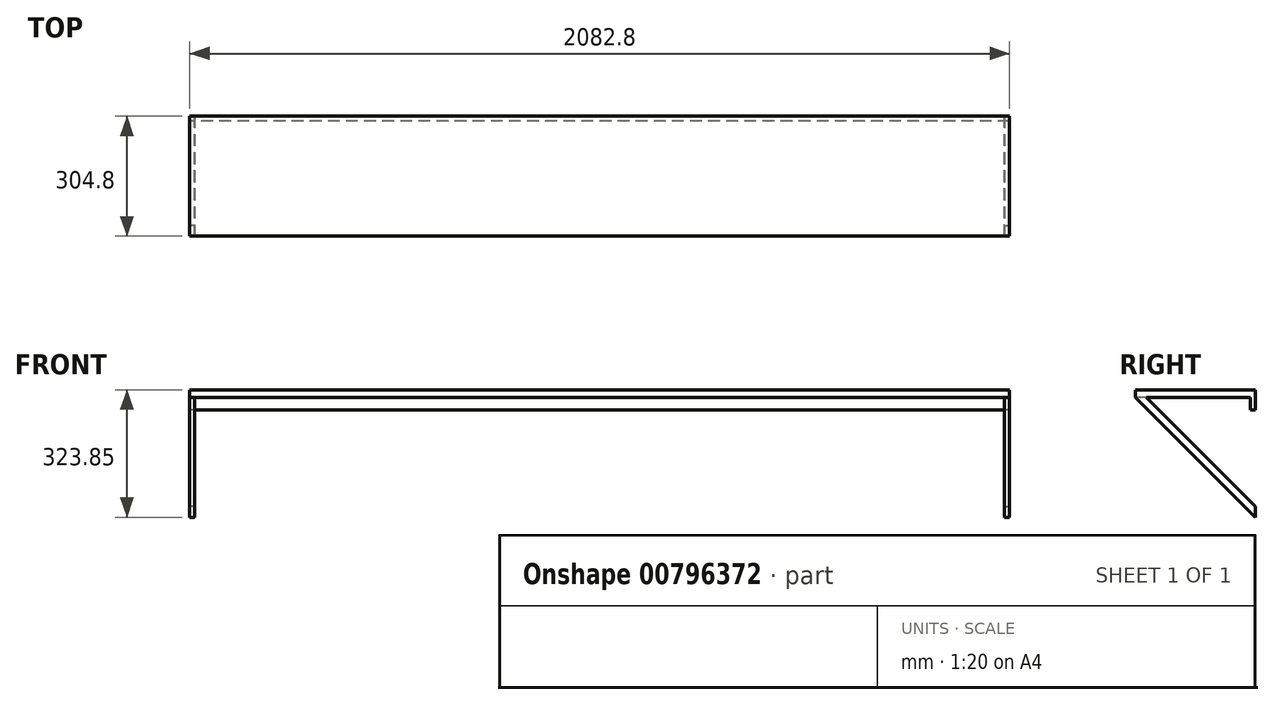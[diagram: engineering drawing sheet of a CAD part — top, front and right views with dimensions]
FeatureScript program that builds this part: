
annotation { "Feature Type Name" : "Feature", "Feature Type Description" : "" }
export const myFeature = defineFeature(function(context is Context, id is Id, definition is map)
    precondition{}
    {
        {
            var Q0;
            Q0=qCreatedBy(makeId("Top.planeOp"),FACE);
            var sketch = newSketch(context, id + "F0", { "sketchPlane" : qUnion([Q0])});
            skLineSegment(sketch, "E0.bottom", {"start": v(0, 0) * mm, "end": v(2082.8, 0) * mm});
            skLineSegment(sketch, "E0.top", {"start": v(0, -304.8) * mm, "end": v(2082.8, -304.8) * mm});
            skLineSegment(sketch, "E0.left", {"start": v(0, 0) * mm, "end": v(0, -304.8) * mm});
            skLineSegment(sketch, "E0.right", {"start": v(2082.8, 0) * mm, "end": v(2082.8, -304.8) * mm});
            skSolve(sketch);
        }
        {
            var Q0;
            Q0=makeQuery(id+"F0.imprint","IMPRINT",FACE,{"disambiguationData":[TD([[makeQuery(id+"F0.imprint","IMPRINT",EDGE,{"derivedFrom":sQuery(id+"F0.wireOp",EDGE,"E0.bottom")}),-1.0]])]});
            extrude(context, id + "F1", {"entities" : qUnion([Q0]), "depth" : 19.05 * mm, "offsetDistance" : 25.4 * mm});
        }
        {
            var Q0;
            Q0=qCreatedBy(makeId("Right.planeOp"),FACE);
            var sketch = newSketch(context, id + "F2", { "sketchPlane" : qUnion([Q0])});
            skLineSegment(sketch, "E1.bottom", {"start": v(0, 0) * mm, "end": v(-12.7, 0) * mm});
            skLineSegment(sketch, "E1.top", {"start": v(0, -31.75) * mm, "end": v(-12.7, -31.75) * mm});
            skLineSegment(sketch, "E1.left", {"start": v(0, 0) * mm, "end": v(0, -31.75) * mm});
            skLineSegment(sketch, "E1.right", {"start": v(-12.7, 0) * mm, "end": v(-12.7, -31.75) * mm});
            skSolve(sketch);
        }
        {
            var Q0;
            Q0=makeQuery(id+"F2.imprint","IMPRINT",FACE,{"disambiguationData":[TD([[makeQuery(id+"F2.imprint","IMPRINT",EDGE,{"derivedFrom":sQuery(id+"F2.wireOp",EDGE,"E1.bottom")}),1.0]])]});
            var Q1;
            Q1=makeQuery(id+"F1.opExtrude","SWEPT_FACE",FACE,{"disambiguationData":[OSD([sQuery(id+"F0.wireOp",EDGE,"E0.right")])]});
            extrude(context, id + "F3", {"entities" : qUnion([Q0]), "operationType" : NewBodyOperationType.ADD, "endBound" : BoundingType.UP_TO_SURFACE, "depth" : 25.4 * mm, "endBoundEntityFace" : qUnion([Q1]), "offsetDistance" : 25.4 * mm});
        }
        {
            var Q0;
            Q0=qCreatedBy(makeId("Right.planeOp"),FACE);
            var sketch = newSketch(context, id + "F4", { "sketchPlane" : qUnion([Q0])});
            skLineSegment(sketch, "E2.0", {"start": v(-12.7, 0) * mm, "end": v(-304.8, 0) * mm, "construction": true});
            skLineSegment(sketch, "E3", {"start": v(-304.8, 0) * mm, "end": v(0, -304.8) * mm});
            skLineSegment(sketch, "E4", {"start": v(0, -304.8) * mm, "end": v(0, -277.86) * mm});
            skLineSegment(sketch, "E5", {"start": v(0, -277.86) * mm, "end": v(-277.86, 0) * mm});
            skLineSegment(sketch, "E6", {"start": v(-277.86, 0) * mm, "end": v(-304.8, 0) * mm});
            skSolve(sketch);
        }
        {
            var Q0;
            Q0=makeQuery(id+"F4.imprint","IMPRINT",FACE,{"disambiguationData":[TD([[makeQuery(id+"F4.imprint","IMPRINT",EDGE,{"derivedFrom":sQuery(id+"F4.wireOp",EDGE,"E3")}),1.0]])]});
            extrude(context, id + "F5", {"entities" : qUnion([Q0]), "operationType" : NewBodyOperationType.ADD, "depth" : 12.7 * mm, "offsetDistance" : 25.4 * mm});
        }
        {
            var Q0;
            Q0=makeQuery(id+"F3.boolean.opBoolean","MERGE",FACE,{"derivedFrom":[makeQuery(id+"F1.opExtrude","SWEPT_FACE",FACE,{"disambiguationData":[OSD([sQuery(id+"F0.wireOp",EDGE,"E0.right")])]}),makeQuery(id+"F3.opExtrude","CAP_FACE",FACE,{"disambiguationData":[OSD([sQuery(id+"F2.wireOp",EDGE,"E1.bottom"),sQuery(id+"F2.wireOp",EDGE,"E1.top"),sQuery(id+"F2.wireOp",EDGE,"E1.left"),sQuery(id+"F2.wireOp",EDGE,"E1.right")])],"isStart":false})]});
            var sketch = newSketch(context, id + "F6", { "sketchPlane" : qUnion([Q0])});
            skLineSegment(sketch, "E7.0.0", {"start": v(0, -277.86) * mm, "end": v(-277.86, 0) * mm});
            skLineSegment(sketch, "E7.0.1", {"start": v(-277.86, 0) * mm, "end": v(-304.8, 0) * mm});
            skLineSegment(sketch, "E7.0.2", {"start": v(-304.8, 0) * mm, "end": v(0, -304.8) * mm});
            skLineSegment(sketch, "E7.0.3", {"start": v(0, -304.8) * mm, "end": v(0, -277.86) * mm});
            skSolve(sketch);
        }
        {
            var Q0;
            Q0=makeQuery(id+"F6.imprint","IMPRINT",FACE,{"disambiguationData":[TD([[makeQuery(id+"F6.imprint","IMPRINT",EDGE,{"derivedFrom":sQuery(id+"F6.wireOp",EDGE,"E7.0.0")}),1.0]])]});
            extrude(context, id + "F7", {"entities" : qUnion([Q0]), "operationType" : NewBodyOperationType.ADD, "oppositeDirection" : true, "depth" : 12.7 * mm, "offsetDistance" : 25.4 * mm});
        }
    });
